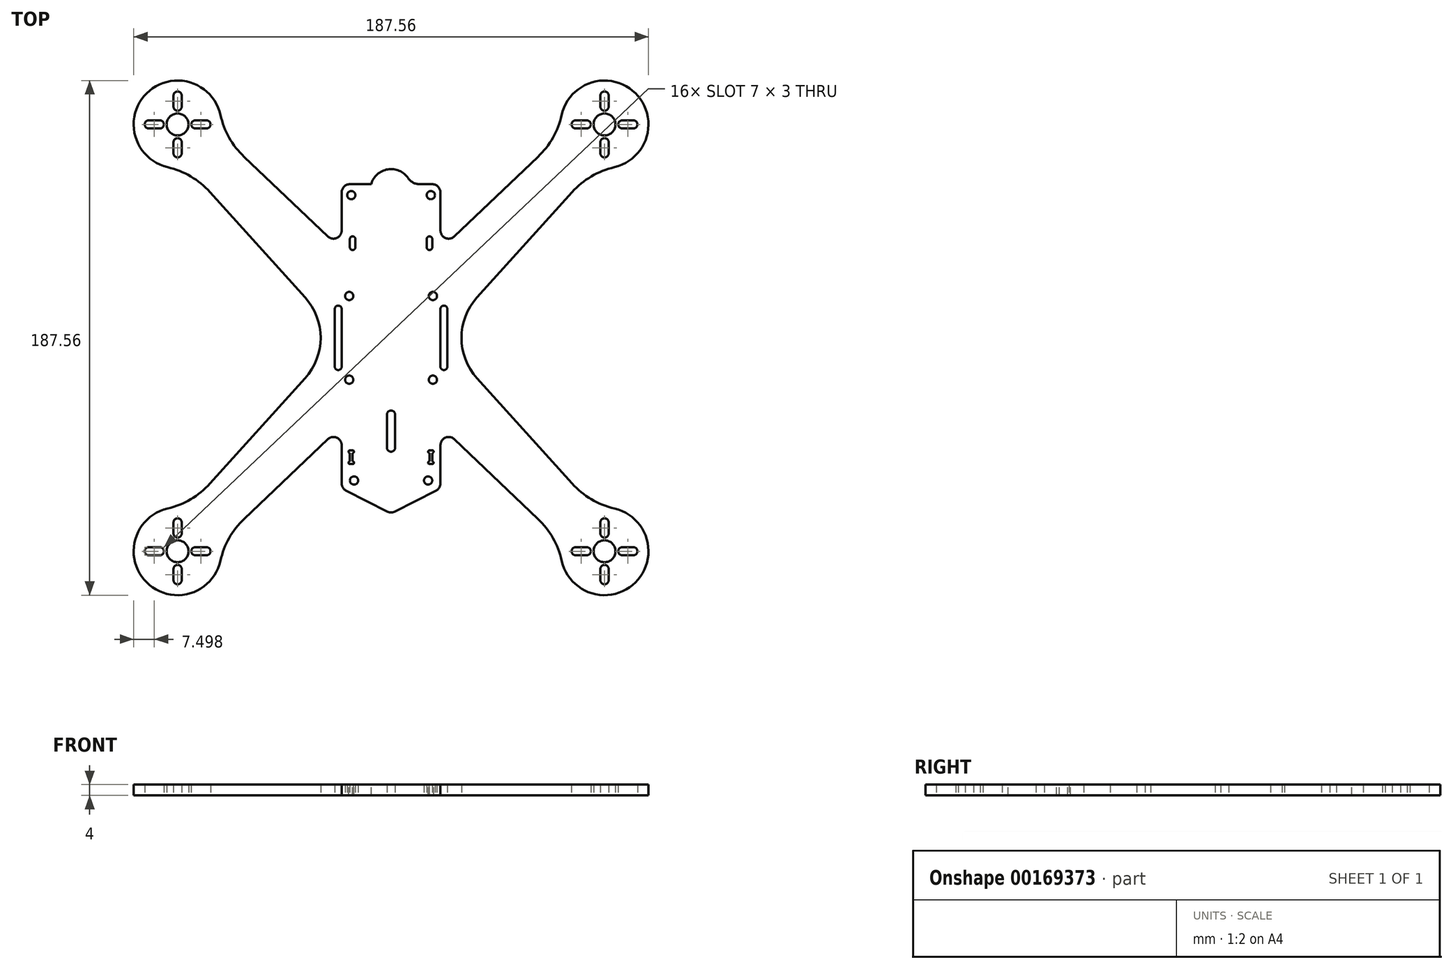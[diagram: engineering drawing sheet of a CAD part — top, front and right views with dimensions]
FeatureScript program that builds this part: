
annotation { "Feature Type Name" : "Feature", "Feature Type Description" : "" }
export const myFeature = defineFeature(function(context is Context, id is Id, definition is map)
    precondition{}
    {
        {
            var Q0;
            Q0=qCreatedBy(makeId("Top.planeOp"),FACE);
            var sketch = newSketch(context, id + "F0", { "sketchPlane" : qUnion([Q0])});
            skLineSegment(sketch, "E0.bottom", {"start": v(-15, 56) * mm, "end": v(15, 56) * mm});
            skLineSegment(sketch, "E0.left", {"start": v(-18, 53) * mm, "end": v(-18, 39.14) * mm});
            skLineSegment(sketch, "E0.right", {"start": v(18, 53) * mm, "end": v(18, 39.14) * mm});
            skCircle(sketch, "E1", {"center": v(0, 0) * mm, "radius": 110 * mm, "construction": true});
            skLineSegment(sketch, "E2", {"start": v(0, 0) * mm, "end": v(-77.78, 77.78) * mm, "construction": true});
            skLineSegment(sketch, "E3", {"start": v(0, 0) * mm, "end": v(-77.78, -77.78) * mm, "construction": true});
            skLineSegment(sketch, "E4", {"start": v(0, 0) * mm, "end": v(77.78, 77.78) * mm, "construction": true});
            skLineSegment(sketch, "E5", {"start": v(0, 0) * mm, "end": v(77.78, -77.78) * mm, "construction": true});
            skCircle(sketch, "E6", {"center": v(-77.78, 77.78) * mm, "radius": 63.5 * mm, "construction": true});
            skCircle(sketch, "E7", {"center": v(-77.78, -77.78) * mm, "radius": 63.5 * mm, "construction": true});
            skCircle(sketch, "E8", {"center": v(77.78, -77.78) * mm, "radius": 63.5 * mm, "construction": true});
            skCircle(sketch, "E9", {"center": v(77.78, 77.78) * mm, "radius": 63.5 * mm, "construction": true});
            skLineSegment(sketch, "E10.trimOffspring", {"start": v(-18, -39.14) * mm, "end": v(-18, -53) * mm});
            skLineSegment(sketch, "E11.trimOffspring", {"start": v(18, -39.14) * mm, "end": v(18, -53) * mm});
            skCircle(sketch, "E12", {"center": v(-15.25, 15.25) * mm, "radius": 1.5 * mm});
            skCircle(sketch, "E13.0.1.0", {"center": v(-15.25, -15.25) * mm, "radius": 1.5 * mm});
            skCircle(sketch, "E13.1.0.0", {"center": v(15.25, 15.25) * mm, "radius": 1.5 * mm});
            skCircle(sketch, "E13.1.1.0", {"center": v(15.25, -15.25) * mm, "radius": 1.5 * mm});
            skLineSegment(sketch, "E13.direction1", {"start": v(-15.25, 15.25) * mm, "end": v(15.25, 15.25) * mm, "construction": true});
            skLineSegment(sketch, "E13.direction2", {"start": v(-15.25, 15.25) * mm, "end": v(-15.25, -15.25) * mm, "construction": true});
            skPoint(sketch, "E14.visualSharp", {"position": v(-18, -32.14) * mm});
            skPoint(sketch, "E15.visualSharp", {"position": v(18, -32.14) * mm});
            skPoint(sketch, "E16.visualSharp", {"position": v(18, 32.14) * mm});
            skPoint(sketch, "E17.visualSharp", {"position": v(-18, 32.14) * mm});
            skCircle(sketch, "E18", {"center": v(-13.5, -52) * mm, "radius": 1.5 * mm});
            skCircle(sketch, "E19", {"center": v(-14.5, 52) * mm, "radius": 1.5 * mm});
            skCircle(sketch, "E20.1.0.0", {"center": v(14.5, 52) * mm, "radius": 1.5 * mm});
            skLineSegment(sketch, "E21", {"start": v(-14.5, 52) * mm, "end": v(14.5, 52) * mm, "construction": true});
            skCircle(sketch, "E22.1.0.0", {"center": v(13.5, -52) * mm, "radius": 1.5 * mm});
            skLineSegment(sketch, "E22.direction1", {"start": v(-13.5, -52) * mm, "end": v(13.5, -52) * mm, "construction": true});
            skPoint(sketch, "E23.visualSharp", {"position": v(-18, 56) * mm});
            skArc(sketch, "E23.filletArc", {"start": v(-15, 56) * mm, "mid": v(-17.12, 55.12) * mm, "end": v(-18, 53) * mm});
            skPoint(sketch, "E24.visualSharp", {"position": v(18, 56) * mm});
            skArc(sketch, "E24.filletArc", {"start": v(18, 53) * mm, "mid": v(17.12, 55.12) * mm, "end": v(15, 56) * mm});
            skArc(sketch, "E25", {"start": v(-81.43, -62.2) * mm, "mid": v(-89.03, -89.16) * mm, "end": v(-62.16, -81.24) * mm});
            skArc(sketch, "E26", {"start": v(62.16, -81.24) * mm, "mid": v(89.03, -89.16) * mm, "end": v(81.43, -62.2) * mm});
            skArc(sketch, "E27", {"start": v(81.43, 62.2) * mm, "mid": v(89.03, 89.16) * mm, "end": v(62.16, 81.24) * mm});
            skArc(sketch, "E28", {"start": v(-62.16, 81.24) * mm, "mid": v(-89.03, 89.16) * mm, "end": v(-81.43, 62.2) * mm});
            skLineSegment(sketch, "E29", {"start": v(-31.33, 14.75) * mm, "end": v(-66, 53.1) * mm});
            skLineSegment(sketch, "E30", {"start": v(-23.07, 36.97) * mm, "end": v(-53.55, 65.99) * mm});
            skPoint(sketch, "E31.visualSharp", {"position": v(-62.19, 74.2) * mm});
            skArc(sketch, "E31.filletArc", {"start": v(-62.16, 81.24) * mm, "mid": v(-59, 72.97) * mm, "end": v(-53.55, 65.99) * mm});
            skPoint(sketch, "E32.visualSharp", {"position": v(-74.2, 62.19) * mm});
            skArc(sketch, "E32.filletArc", {"start": v(-66, 53.1) * mm, "mid": v(-73.02, 58.83) * mm, "end": v(-81.43, 62.2) * mm});
            skLineSegment(sketch, "E33", {"start": v(23.07, 36.97) * mm, "end": v(53.55, 65.99) * mm});
            skLineSegment(sketch, "E34", {"start": v(31.33, 14.75) * mm, "end": v(66, 53.1) * mm});
            skPoint(sketch, "E35.visualSharp", {"position": v(62.19, 74.2) * mm});
            skArc(sketch, "E35.filletArc", {"start": v(53.55, 65.99) * mm, "mid": v(59, 72.97) * mm, "end": v(62.16, 81.24) * mm});
            skPoint(sketch, "E36.visualSharp", {"position": v(74.2, 62.19) * mm});
            skArc(sketch, "E36.filletArc", {"start": v(81.43, 62.2) * mm, "mid": v(73.02, 58.83) * mm, "end": v(66, 53.1) * mm});
            skLineSegment(sketch, "E37", {"start": v(-31.33, -14.75) * mm, "end": v(-66, -53.1) * mm});
            skLineSegment(sketch, "E38", {"start": v(-53.55, -65.99) * mm, "end": v(-23.07, -36.97) * mm});
            skLineSegment(sketch, "E39", {"start": v(23.07, -36.97) * mm, "end": v(53.55, -65.99) * mm});
            skLineSegment(sketch, "E40", {"start": v(66, -53.1) * mm, "end": v(31.33, -14.75) * mm});
            skPoint(sketch, "E41.visualSharp", {"position": v(-74.2, -62.19) * mm});
            skArc(sketch, "E41.filletArc", {"start": v(-81.43, -62.2) * mm, "mid": v(-73.02, -58.83) * mm, "end": v(-66, -53.1) * mm});
            skPoint(sketch, "E42.visualSharp", {"position": v(-62.19, -74.2) * mm});
            skArc(sketch, "E42.filletArc", {"start": v(-53.55, -65.99) * mm, "mid": v(-59, -72.97) * mm, "end": v(-62.16, -81.24) * mm});
            skPoint(sketch, "E43.visualSharp", {"position": v(62.19, -74.2) * mm});
            skArc(sketch, "E43.filletArc", {"start": v(62.16, -81.24) * mm, "mid": v(59, -72.97) * mm, "end": v(53.55, -65.99) * mm});
            skPoint(sketch, "E44.visualSharp", {"position": v(74.2, -62.19) * mm});
            skArc(sketch, "E44.filletArc", {"start": v(66, -53.1) * mm, "mid": v(73.02, -58.83) * mm, "end": v(81.43, -62.2) * mm});
            skCircle(sketch, "E45", {"center": v(-77.78, 77.78) * mm, "radius": 4 * mm});
            skCircle(sketch, "E46", {"center": v(77.78, 77.78) * mm, "radius": 4 * mm});
            skCircle(sketch, "E47", {"center": v(77.78, -77.78) * mm, "radius": 4 * mm});
            skCircle(sketch, "E48", {"center": v(-77.78, -77.78) * mm, "radius": 4 * mm});
            skArc(sketch, "E49", {"start": v(1.5, -28) * mm, "mid": v(0, -26.5) * mm, "end": v(-1.5, -28) * mm});
            skArc(sketch, "E50", {"start": v(-1.5, -40) * mm, "mid": v(0, -41.5) * mm, "end": v(1.5, -40) * mm});
            skLineSegment(sketch, "E51", {"start": v(-1.5, -28) * mm, "end": v(-1.5, -40) * mm});
            skLineSegment(sketch, "E52", {"start": v(1.5, -28) * mm, "end": v(1.5, -40) * mm});
            skArc(sketch, "E53.filletArc", {"start": v(-18, -39.14) * mm, "mid": v(-19.82, -36.38) * mm, "end": v(-23.07, -36.97) * mm});
            skArc(sketch, "E54.filletArc", {"start": v(23.07, -36.97) * mm, "mid": v(19.82, -36.38) * mm, "end": v(18, -39.14) * mm});
            skArc(sketch, "E55.filletArc", {"start": v(-23.07, 36.97) * mm, "mid": v(-19.82, 36.38) * mm, "end": v(-18, 39.14) * mm});
            skArc(sketch, "E56.filletArc", {"start": v(18, 39.14) * mm, "mid": v(19.82, 36.38) * mm, "end": v(23.07, 36.97) * mm});
            skArc(sketch, "E57", {"start": v(-13, 36) * mm, "mid": v(-14, 37) * mm, "end": v(-15, 36) * mm});
            skArc(sketch, "E58", {"start": v(-15, 33) * mm, "mid": v(-14, 32) * mm, "end": v(-13, 33) * mm});
            skLineSegment(sketch, "E59", {"start": v(-14, 36) * mm, "end": v(-14, 33) * mm, "construction": true});
            skLineSegment(sketch, "E60", {"start": v(-15, 36) * mm, "end": v(-15, 33) * mm});
            skLineSegment(sketch, "E61", {"start": v(-13, 36) * mm, "end": v(-13, 33) * mm});
            skLineSegment(sketch, "E62.MirrorCS", {"start": v(14, 36) * mm, "end": v(14, 33) * mm, "construction": true});
            skArc(sketch, "E63.MirrorCS", {"start": v(13, 36) * mm, "mid": v(14, 37) * mm, "end": v(15, 36) * mm});
            skArc(sketch, "E64.MirrorCS", {"start": v(15, 33) * mm, "mid": v(14, 32) * mm, "end": v(13, 33) * mm});
            skLineSegment(sketch, "E65.MirrorCS", {"start": v(13, 36) * mm, "end": v(13, 33) * mm});
            skLineSegment(sketch, "E66.MirrorCS", {"start": v(15, 36) * mm, "end": v(15, 33) * mm});
            skPoint(sketch, "E67.visualSharp", {"position": v(-18, 0) * mm});
            skArc(sketch, "E67.filletArc", {"start": v(-31.33, -14.75) * mm, "mid": v(-25.65, 0) * mm, "end": v(-31.33, 14.75) * mm});
            skPoint(sketch, "E68.visualSharp", {"position": v(18, 0) * mm});
            skArc(sketch, "E68.filletArc", {"start": v(31.33, 14.75) * mm, "mid": v(25.65, 0) * mm, "end": v(31.33, -14.75) * mm});
            skLineSegment(sketch, "E69.left", {"start": v(-20.5, 10.5) * mm, "end": v(-20.5, -10.5) * mm});
            skLineSegment(sketch, "E69.right", {"start": v(-18, 10.5) * mm, "end": v(-18, -10.5) * mm});
            skArc(sketch, "E70", {"start": v(-18, 10.5) * mm, "mid": v(-19.25, 11.75) * mm, "end": v(-20.5, 10.5) * mm});
            skArc(sketch, "E71", {"start": v(-20.5, -10.5) * mm, "mid": v(-19.25, -11.75) * mm, "end": v(-18, -10.5) * mm});
            skArc(sketch, "E72.MirrorCS", {"start": v(20.5, -10.5) * mm, "mid": v(19.25, -11.75) * mm, "end": v(18, -10.5) * mm});
            skLineSegment(sketch, "E73.MirrorCS", {"start": v(20.5, 10.5) * mm, "end": v(20.5, -10.5) * mm});
            skArc(sketch, "E74.MirrorCS", {"start": v(18, 10.5) * mm, "mid": v(19.25, 11.75) * mm, "end": v(20.5, 10.5) * mm});
            skLineSegment(sketch, "E75.MirrorCS", {"start": v(18, 10.5) * mm, "end": v(18, -10.5) * mm});
            skLineSegment(sketch, "E76", {"start": v(-15, -56) * mm, "end": v(15, -56) * mm});
            skPoint(sketch, "E77.visualSharp", {"position": v(-18, -56) * mm});
            skArc(sketch, "E77.filletArc", {"start": v(-18, -53) * mm, "mid": v(-17.12, -55.12) * mm, "end": v(-15, -56) * mm});
            skPoint(sketch, "E78.visualSharp", {"position": v(18, -56) * mm});
            skArc(sketch, "E78.filletArc", {"start": v(15, -56) * mm, "mid": v(17.12, -55.12) * mm, "end": v(18, -53) * mm});
            skLineSegment(sketch, "E79", {"start": v(-77.78, 77.78) * mm, "end": v(-89.03, 89.16) * mm, "construction": true});
            skLineSegment(sketch, "E80", {"start": v(-77.78, 77.78) * mm, "end": v(-89.1, 66.47) * mm, "construction": true});
            skLineSegment(sketch, "E81", {"start": v(-77.78, 77.78) * mm, "end": v(-66.47, 89.1) * mm, "construction": true});
            skArc(sketch, "E82", {"start": v(-79.28, 84.28) * mm, "mid": v(-77.78, 82.78) * mm, "end": v(-76.28, 84.28) * mm});
            skArc(sketch, "E83", {"start": v(-76.28, 88.28) * mm, "mid": v(-77.78, 89.78) * mm, "end": v(-79.28, 88.28) * mm});
            skLineSegment(sketch, "E84", {"start": v(-79.28, 88.28) * mm, "end": v(-79.28, 84.28) * mm});
            skLineSegment(sketch, "E85", {"start": v(-76.28, 88.28) * mm, "end": v(-76.28, 84.28) * mm});
            skLineSegment(sketch, "E86", {"start": v(-77.78, 77.78) * mm, "end": v(-77.78, 93.78) * mm, "construction": true});
            skArc(sketch, "E87.1.0", {"start": v(-88.28, 79.28) * mm, "mid": v(-89.78, 77.78) * mm, "end": v(-88.28, 76.28) * mm});
            skArc(sketch, "E87.1.1", {"start": v(-84.28, 76.28) * mm, "mid": v(-82.78, 77.78) * mm, "end": v(-84.28, 79.28) * mm});
            skLineSegment(sketch, "E87.1.2", {"start": v(-88.28, 79.28) * mm, "end": v(-84.28, 79.28) * mm});
            skLineSegment(sketch, "E87.1.3", {"start": v(-88.28, 76.28) * mm, "end": v(-84.28, 76.28) * mm});
            skArc(sketch, "E87.2.0", {"start": v(-79.28, 67.28) * mm, "mid": v(-77.78, 65.78) * mm, "end": v(-76.28, 67.28) * mm});
            skArc(sketch, "E87.2.1", {"start": v(-76.28, 71.28) * mm, "mid": v(-77.78, 72.78) * mm, "end": v(-79.28, 71.28) * mm});
            skLineSegment(sketch, "E87.2.2", {"start": v(-79.28, 67.28) * mm, "end": v(-79.28, 71.28) * mm});
            skLineSegment(sketch, "E87.2.3", {"start": v(-76.28, 67.28) * mm, "end": v(-76.28, 71.28) * mm});
            skArc(sketch, "E87.3.0", {"start": v(-67.28, 76.28) * mm, "mid": v(-65.78, 77.78) * mm, "end": v(-67.28, 79.28) * mm});
            skArc(sketch, "E87.3.1", {"start": v(-71.28, 79.28) * mm, "mid": v(-72.78, 77.78) * mm, "end": v(-71.28, 76.28) * mm});
            skLineSegment(sketch, "E87.3.2", {"start": v(-67.28, 76.28) * mm, "end": v(-71.28, 76.28) * mm});
            skLineSegment(sketch, "E87.3.3", {"start": v(-67.28, 79.28) * mm, "end": v(-71.28, 79.28) * mm});
            skLineSegment(sketch, "E88.1.0", {"start": v(-88.28, -79.28) * mm, "end": v(-84.28, -79.28) * mm});
            skArc(sketch, "E88.1.1", {"start": v(-88.28, -76.28) * mm, "mid": v(-89.78, -77.78) * mm, "end": v(-88.28, -79.28) * mm});
            skLineSegment(sketch, "E88.1.2", {"start": v(-88.28, -76.28) * mm, "end": v(-84.28, -76.28) * mm});
            skArc(sketch, "E88.1.3", {"start": v(-84.28, -79.28) * mm, "mid": v(-82.78, -77.78) * mm, "end": v(-84.28, -76.28) * mm});
            skArc(sketch, "E88.1.4", {"start": v(-76.28, -67.28) * mm, "mid": v(-77.78, -65.78) * mm, "end": v(-79.28, -67.28) * mm});
            skLineSegment(sketch, "E88.1.5", {"start": v(-79.28, -67.28) * mm, "end": v(-79.28, -71.28) * mm});
            skLineSegment(sketch, "E88.1.6", {"start": v(-76.28, -67.28) * mm, "end": v(-76.28, -71.28) * mm});
            skArc(sketch, "E88.1.7", {"start": v(-79.28, -71.28) * mm, "mid": v(-77.78, -72.78) * mm, "end": v(-76.28, -71.28) * mm});
            skLineSegment(sketch, "E88.1.8", {"start": v(-67.28, -79.28) * mm, "end": v(-71.28, -79.28) * mm});
            skArc(sketch, "E88.1.9", {"start": v(-71.28, -76.28) * mm, "mid": v(-72.78, -77.78) * mm, "end": v(-71.28, -79.28) * mm});
            skLineSegment(sketch, "E88.1.10", {"start": v(-67.28, -76.28) * mm, "end": v(-71.28, -76.28) * mm});
            skArc(sketch, "E88.1.11", {"start": v(-67.28, -79.28) * mm, "mid": v(-65.78, -77.78) * mm, "end": v(-67.28, -76.28) * mm});
            skArc(sketch, "E88.1.12", {"start": v(-76.28, -84.28) * mm, "mid": v(-77.78, -82.78) * mm, "end": v(-79.28, -84.28) * mm});
            skLineSegment(sketch, "E88.1.13", {"start": v(-76.28, -88.28) * mm, "end": v(-76.28, -84.28) * mm});
            skLineSegment(sketch, "E88.1.14", {"start": v(-79.28, -88.28) * mm, "end": v(-79.28, -84.28) * mm});
            skArc(sketch, "E88.1.15", {"start": v(-79.28, -88.28) * mm, "mid": v(-77.78, -89.78) * mm, "end": v(-76.28, -88.28) * mm});
            skLineSegment(sketch, "E88.2.0", {"start": v(79.28, -88.28) * mm, "end": v(79.28, -84.28) * mm});
            skArc(sketch, "E88.2.1", {"start": v(76.28, -88.28) * mm, "mid": v(77.78, -89.78) * mm, "end": v(79.28, -88.28) * mm});
            skLineSegment(sketch, "E88.2.2", {"start": v(76.28, -88.28) * mm, "end": v(76.28, -84.28) * mm});
            skArc(sketch, "E88.2.3", {"start": v(79.28, -84.28) * mm, "mid": v(77.78, -82.78) * mm, "end": v(76.28, -84.28) * mm});
            skArc(sketch, "E88.2.4", {"start": v(67.28, -76.28) * mm, "mid": v(65.78, -77.78) * mm, "end": v(67.28, -79.28) * mm});
            skLineSegment(sketch, "E88.2.5", {"start": v(67.28, -79.28) * mm, "end": v(71.28, -79.28) * mm});
            skLineSegment(sketch, "E88.2.6", {"start": v(67.28, -76.28) * mm, "end": v(71.28, -76.28) * mm});
            skArc(sketch, "E88.2.7", {"start": v(71.28, -79.28) * mm, "mid": v(72.78, -77.78) * mm, "end": v(71.28, -76.28) * mm});
            skLineSegment(sketch, "E88.2.8", {"start": v(79.28, -67.28) * mm, "end": v(79.28, -71.28) * mm});
            skArc(sketch, "E88.2.9", {"start": v(76.28, -71.28) * mm, "mid": v(77.78, -72.78) * mm, "end": v(79.28, -71.28) * mm});
            skLineSegment(sketch, "E88.2.10", {"start": v(76.28, -67.28) * mm, "end": v(76.28, -71.28) * mm});
            skArc(sketch, "E88.2.11", {"start": v(79.28, -67.28) * mm, "mid": v(77.78, -65.78) * mm, "end": v(76.28, -67.28) * mm});
            skArc(sketch, "E88.2.12", {"start": v(84.28, -76.28) * mm, "mid": v(82.78, -77.78) * mm, "end": v(84.28, -79.28) * mm});
            skLineSegment(sketch, "E88.2.13", {"start": v(88.28, -76.28) * mm, "end": v(84.28, -76.28) * mm});
            skLineSegment(sketch, "E88.2.14", {"start": v(88.28, -79.28) * mm, "end": v(84.28, -79.28) * mm});
            skArc(sketch, "E88.2.15", {"start": v(88.28, -79.28) * mm, "mid": v(89.78, -77.78) * mm, "end": v(88.28, -76.28) * mm});
            skLineSegment(sketch, "E88.3.0", {"start": v(88.28, 79.28) * mm, "end": v(84.28, 79.28) * mm});
            skArc(sketch, "E88.3.1", {"start": v(88.28, 76.28) * mm, "mid": v(89.78, 77.78) * mm, "end": v(88.28, 79.28) * mm});
            skLineSegment(sketch, "E88.3.2", {"start": v(88.28, 76.28) * mm, "end": v(84.28, 76.28) * mm});
            skArc(sketch, "E88.3.3", {"start": v(84.28, 79.28) * mm, "mid": v(82.78, 77.78) * mm, "end": v(84.28, 76.28) * mm});
            skArc(sketch, "E88.3.4", {"start": v(76.28, 67.28) * mm, "mid": v(77.78, 65.78) * mm, "end": v(79.28, 67.28) * mm});
            skLineSegment(sketch, "E88.3.5", {"start": v(79.28, 67.28) * mm, "end": v(79.28, 71.28) * mm});
            skLineSegment(sketch, "E88.3.6", {"start": v(76.28, 67.28) * mm, "end": v(76.28, 71.28) * mm});
            skArc(sketch, "E88.3.7", {"start": v(79.28, 71.28) * mm, "mid": v(77.78, 72.78) * mm, "end": v(76.28, 71.28) * mm});
            skLineSegment(sketch, "E88.3.8", {"start": v(67.28, 79.28) * mm, "end": v(71.28, 79.28) * mm});
            skArc(sketch, "E88.3.9", {"start": v(71.28, 76.28) * mm, "mid": v(72.78, 77.78) * mm, "end": v(71.28, 79.28) * mm});
            skLineSegment(sketch, "E88.3.10", {"start": v(67.28, 76.28) * mm, "end": v(71.28, 76.28) * mm});
            skArc(sketch, "E88.3.11", {"start": v(67.28, 79.28) * mm, "mid": v(65.78, 77.78) * mm, "end": v(67.28, 76.28) * mm});
            skArc(sketch, "E88.3.12", {"start": v(76.28, 84.28) * mm, "mid": v(77.78, 82.78) * mm, "end": v(79.28, 84.28) * mm});
            skLineSegment(sketch, "E88.3.13", {"start": v(76.28, 88.28) * mm, "end": v(76.28, 84.28) * mm});
            skLineSegment(sketch, "E88.3.14", {"start": v(79.28, 88.28) * mm, "end": v(79.28, 84.28) * mm});
            skArc(sketch, "E88.3.15", {"start": v(79.28, 88.28) * mm, "mid": v(77.78, 89.78) * mm, "end": v(76.28, 88.28) * mm});
            skLineSegment(sketch, "E89", {"start": v(-93.78, -77.78) * mm, "end": v(-61.17, -77.78) * mm, "construction": true});
            skLineSegment(sketch, "E90", {"start": v(-77.78, -93.78) * mm, "end": v(-77.78, -61.1) * mm, "construction": true});
            skPoint(sketch, "E90.endSnap0", {"position": v(-77.78, -65.78) * mm});
            skSolve(sketch);
        }
        {
            var Q0;
            Q0=qSketchRegion(id+"F0",true);
            extrude(context, id + "F1", {"entities" : qUnion([Q0]), "depth" : 4 * mm});
        }
        {
            var Q0;
            Q0=makeQuery(id+"F1.opExtrude","CAP_FACE",FACE,{"disambiguationData":[OSD([sQuery(id+"F0.wireOp",EDGE,"E0.bottom"),sQuery(id+"F0.wireOp",EDGE,"E0.left"),sQuery(id+"F0.wireOp",EDGE,"E0.right"),sQuery(id+"F0.wireOp",EDGE,"E10.trimOffspring"),sQuery(id+"F0.wireOp",EDGE,"E11.trimOffspring"),sQuery(id+"F0.wireOp",EDGE,"E12"),sQuery(id+"F0.wireOp",EDGE,"E13.0.1.0"),sQuery(id+"F0.wireOp",EDGE,"E13.1.0.0"),sQuery(id+"F0.wireOp",EDGE,"E13.1.1.0"),sQuery(id+"F0.wireOp",EDGE,"E18"),sQuery(id+"F0.wireOp",EDGE,"E19"),sQuery(id+"F0.wireOp",EDGE,"E20.1.0.0"),sQuery(id+"F0.wireOp",EDGE,"E22.1.0.0"),sQuery(id+"F0.wireOp",EDGE,"E23.filletArc"),sQuery(id+"F0.wireOp",EDGE,"E24.filletArc"),sQuery(id+"F0.wireOp",EDGE,"E25"),sQuery(id+"F0.wireOp",EDGE,"E26"),sQuery(id+"F0.wireOp",EDGE,"E27"),sQuery(id+"F0.wireOp",EDGE,"E28"),sQuery(id+"F0.wireOp",EDGE,"E29"),sQuery(id+"F0.wireOp",EDGE,"E30"),sQuery(id+"F0.wireOp",EDGE,"E31.filletArc"),sQuery(id+"F0.wireOp",EDGE,"E32.filletArc"),sQuery(id+"F0.wireOp",EDGE,"E33"),sQuery(id+"F0.wireOp",EDGE,"E34"),sQuery(id+"F0.wireOp",EDGE,"E35.filletArc"),sQuery(id+"F0.wireOp",EDGE,"E36.filletArc"),sQuery(id+"F0.wireOp",EDGE,"E37"),sQuery(id+"F0.wireOp",EDGE,"E38"),sQuery(id+"F0.wireOp",EDGE,"E39"),sQuery(id+"F0.wireOp",EDGE,"E40"),sQuery(id+"F0.wireOp",EDGE,"E41.filletArc"),sQuery(id+"F0.wireOp",EDGE,"E42.filletArc"),sQuery(id+"F0.wireOp",EDGE,"E43.filletArc"),sQuery(id+"F0.wireOp",EDGE,"E44.filletArc"),sQuery(id+"F0.wireOp",EDGE,"E45"),sQuery(id+"F0.wireOp",EDGE,"E46"),sQuery(id+"F0.wireOp",EDGE,"E47"),sQuery(id+"F0.wireOp",EDGE,"E48"),sQuery(id+"F0.wireOp",EDGE,"E49"),sQuery(id+"F0.wireOp",EDGE,"E50"),sQuery(id+"F0.wireOp",EDGE,"E51"),sQuery(id+"F0.wireOp",EDGE,"E52"),sQuery(id+"F0.wireOp",EDGE,"E53.filletArc"),sQuery(id+"F0.wireOp",EDGE,"E54.filletArc"),sQuery(id+"F0.wireOp",EDGE,"E55.filletArc"),sQuery(id+"F0.wireOp",EDGE,"E56.filletArc"),sQuery(id+"F0.wireOp",EDGE,"E57"),sQuery(id+"F0.wireOp",EDGE,"E58"),sQuery(id+"F0.wireOp",EDGE,"E60"),sQuery(id+"F0.wireOp",EDGE,"E61"),sQuery(id+"F0.wireOp",EDGE,"E63.MirrorCS"),sQuery(id+"F0.wireOp",EDGE,"E64.MirrorCS"),sQuery(id+"F0.wireOp",EDGE,"E65.MirrorCS"),sQuery(id+"F0.wireOp",EDGE,"E66.MirrorCS"),sQuery(id+"F0.wireOp",EDGE,"E67.filletArc"),sQuery(id+"F0.wireOp",EDGE,"E68.filletArc"),sQuery(id+"F0.wireOp",EDGE,"E69.left"),sQuery(id+"F0.wireOp",EDGE,"E69.right"),sQuery(id+"F0.wireOp",EDGE,"E70"),sQuery(id+"F0.wireOp",EDGE,"E71"),sQuery(id+"F0.wireOp",EDGE,"E72.MirrorCS"),sQuery(id+"F0.wireOp",EDGE,"E73.MirrorCS"),sQuery(id+"F0.wireOp",EDGE,"E74.MirrorCS"),sQuery(id+"F0.wireOp",EDGE,"E75.MirrorCS"),sQuery(id+"F0.wireOp",EDGE,"E76"),sQuery(id+"F0.wireOp",EDGE,"E77.filletArc"),sQuery(id+"F0.wireOp",EDGE,"E78.filletArc"),sQuery(id+"F0.wireOp",EDGE,"E82"),sQuery(id+"F0.wireOp",EDGE,"E83"),sQuery(id+"F0.wireOp",EDGE,"E84"),sQuery(id+"F0.wireOp",EDGE,"E85"),sQuery(id+"F0.wireOp",EDGE,"E87.1.0"),sQuery(id+"F0.wireOp",EDGE,"E87.1.1"),sQuery(id+"F0.wireOp",EDGE,"E87.1.2"),sQuery(id+"F0.wireOp",EDGE,"E87.1.3"),sQuery(id+"F0.wireOp",EDGE,"E87.2.0"),sQuery(id+"F0.wireOp",EDGE,"E87.2.1"),sQuery(id+"F0.wireOp",EDGE,"E87.2.2"),sQuery(id+"F0.wireOp",EDGE,"E87.2.3"),sQuery(id+"F0.wireOp",EDGE,"E87.3.0"),sQuery(id+"F0.wireOp",EDGE,"E87.3.1"),sQuery(id+"F0.wireOp",EDGE,"E87.3.2"),sQuery(id+"F0.wireOp",EDGE,"E87.3.3"),sQuery(id+"F0.wireOp",EDGE,"E88.1.0"),sQuery(id+"F0.wireOp",EDGE,"E88.1.1"),sQuery(id+"F0.wireOp",EDGE,"E88.1.2"),sQuery(id+"F0.wireOp",EDGE,"E88.1.3"),sQuery(id+"F0.wireOp",EDGE,"E88.1.4"),sQuery(id+"F0.wireOp",EDGE,"E88.1.5"),sQuery(id+"F0.wireOp",EDGE,"E88.1.6"),sQuery(id+"F0.wireOp",EDGE,"E88.1.7"),sQuery(id+"F0.wireOp",EDGE,"E88.1.8"),sQuery(id+"F0.wireOp",EDGE,"E88.1.9"),sQuery(id+"F0.wireOp",EDGE,"E88.1.10"),sQuery(id+"F0.wireOp",EDGE,"E88.1.11"),sQuery(id+"F0.wireOp",EDGE,"E88.1.12"),sQuery(id+"F0.wireOp",EDGE,"E88.1.13"),sQuery(id+"F0.wireOp",EDGE,"E88.1.14"),sQuery(id+"F0.wireOp",EDGE,"E88.1.15"),sQuery(id+"F0.wireOp",EDGE,"E88.2.0"),sQuery(id+"F0.wireOp",EDGE,"E88.2.1"),sQuery(id+"F0.wireOp",EDGE,"E88.2.2"),sQuery(id+"F0.wireOp",EDGE,"E88.2.3"),sQuery(id+"F0.wireOp",EDGE,"E88.2.4"),sQuery(id+"F0.wireOp",EDGE,"E88.2.5"),sQuery(id+"F0.wireOp",EDGE,"E88.2.6"),sQuery(id+"F0.wireOp",EDGE,"E88.2.7"),sQuery(id+"F0.wireOp",EDGE,"E88.2.8"),sQuery(id+"F0.wireOp",EDGE,"E88.2.9"),sQuery(id+"F0.wireOp",EDGE,"E88.2.10"),sQuery(id+"F0.wireOp",EDGE,"E88.2.11"),sQuery(id+"F0.wireOp",EDGE,"E88.2.12"),sQuery(id+"F0.wireOp",EDGE,"E88.2.13"),sQuery(id+"F0.wireOp",EDGE,"E88.2.14"),sQuery(id+"F0.wireOp",EDGE,"E88.2.15"),sQuery(id+"F0.wireOp",EDGE,"E88.3.0"),sQuery(id+"F0.wireOp",EDGE,"E88.3.1"),sQuery(id+"F0.wireOp",EDGE,"E88.3.2"),sQuery(id+"F0.wireOp",EDGE,"E88.3.3"),sQuery(id+"F0.wireOp",EDGE,"E88.3.4"),sQuery(id+"F0.wireOp",EDGE,"E88.3.5"),sQuery(id+"F0.wireOp",EDGE,"E88.3.6"),sQuery(id+"F0.wireOp",EDGE,"E88.3.7"),sQuery(id+"F0.wireOp",EDGE,"E88.3.8"),sQuery(id+"F0.wireOp",EDGE,"E88.3.9"),sQuery(id+"F0.wireOp",EDGE,"E88.3.10"),sQuery(id+"F0.wireOp",EDGE,"E88.3.11"),sQuery(id+"F0.wireOp",EDGE,"E88.3.12"),sQuery(id+"F0.wireOp",EDGE,"E88.3.13"),sQuery(id+"F0.wireOp",EDGE,"E88.3.14"),sQuery(id+"F0.wireOp",EDGE,"E88.3.15")])],"isStart":false});
            var sketch = newSketch(context, id + "F2", { "sketchPlane" : qUnion([Q0])});
            skLineSegment(sketch, "E91.bottom", {"start": v(-15, -41) * mm, "end": v(-14, -41) * mm});
            skLineSegment(sketch, "E91.top", {"start": v(-15, -46) * mm, "end": v(-14, -46) * mm});
            skLineSegment(sketch, "E91.right", {"start": v(-14, -42) * mm, "end": v(-14, -45) * mm});
            skArc(sketch, "E92", {"start": v(-14, -46) * mm, "mid": v(-13.5, -45.5) * mm, "end": v(-14, -45) * mm});
            skArc(sketch, "E93", {"start": v(-15, -45) * mm, "mid": v(-15.5, -45.5) * mm, "end": v(-15, -46) * mm});
            skArc(sketch, "E94", {"start": v(-15, -41) * mm, "mid": v(-15.5, -41.5) * mm, "end": v(-15, -42) * mm});
            skArc(sketch, "E95", {"start": v(-14, -42) * mm, "mid": v(-13.5, -41.5) * mm, "end": v(-14, -41) * mm});
            skLineSegment(sketch, "E96.trimOffspring", {"start": v(-15, -42) * mm, "end": v(-15, -45) * mm});
            skArc(sketch, "E97.MirrorCS", {"start": v(15, -45) * mm, "mid": v(15.5, -45.5) * mm, "end": v(15, -46) * mm});
            skLineSegment(sketch, "E98.MirrorCS", {"start": v(15, -46) * mm, "end": v(14, -46) * mm});
            skLineSegment(sketch, "E99.MirrorCS", {"start": v(15, -41) * mm, "end": v(14, -41) * mm});
            skArc(sketch, "E100.MirrorCS", {"start": v(14, -46) * mm, "mid": v(13.5, -45.5) * mm, "end": v(14, -45) * mm});
            skArc(sketch, "E101.MirrorCS", {"start": v(14, -42) * mm, "mid": v(13.5, -41.5) * mm, "end": v(14, -41) * mm});
            skArc(sketch, "E102.MirrorCS", {"start": v(15, -41) * mm, "mid": v(15.5, -41.5) * mm, "end": v(15, -42) * mm});
            skLineSegment(sketch, "E103.MirrorCS", {"start": v(15, -42) * mm, "end": v(15, -45) * mm});
            skLineSegment(sketch, "E104.MirrorCS", {"start": v(14, -42) * mm, "end": v(14, -45) * mm});
            skSolve(sketch);
        }
        {
            var Q0;
            Q0=qSketchRegion(id+"F2",true);
            extrude(context, id + "F3", {"entities" : qUnion([Q0]), "operationType" : NewBodyOperationType.REMOVE, "endBound" : BoundingType.THROUGH_ALL, "oppositeDirection" : true, "depth" : 25 * mm});
        }
        {
            var Q0;
            Q0=makeQuery(id+"F1.opExtrude","CAP_FACE",FACE,{"disambiguationData":[OSD([sQuery(id+"F0.wireOp",EDGE,"E0.bottom"),sQuery(id+"F0.wireOp",EDGE,"E0.left"),sQuery(id+"F0.wireOp",EDGE,"E0.right"),sQuery(id+"F0.wireOp",EDGE,"E10.trimOffspring"),sQuery(id+"F0.wireOp",EDGE,"E11.trimOffspring"),sQuery(id+"F0.wireOp",EDGE,"E12"),sQuery(id+"F0.wireOp",EDGE,"E13.0.1.0"),sQuery(id+"F0.wireOp",EDGE,"E13.1.0.0"),sQuery(id+"F0.wireOp",EDGE,"E13.1.1.0"),sQuery(id+"F0.wireOp",EDGE,"E18"),sQuery(id+"F0.wireOp",EDGE,"E19"),sQuery(id+"F0.wireOp",EDGE,"E20.1.0.0"),sQuery(id+"F0.wireOp",EDGE,"E22.1.0.0"),sQuery(id+"F0.wireOp",EDGE,"E23.filletArc"),sQuery(id+"F0.wireOp",EDGE,"E24.filletArc"),sQuery(id+"F0.wireOp",EDGE,"E25"),sQuery(id+"F0.wireOp",EDGE,"E26"),sQuery(id+"F0.wireOp",EDGE,"E27"),sQuery(id+"F0.wireOp",EDGE,"E28"),sQuery(id+"F0.wireOp",EDGE,"E29"),sQuery(id+"F0.wireOp",EDGE,"E30"),sQuery(id+"F0.wireOp",EDGE,"E31.filletArc"),sQuery(id+"F0.wireOp",EDGE,"E32.filletArc"),sQuery(id+"F0.wireOp",EDGE,"E33"),sQuery(id+"F0.wireOp",EDGE,"E34"),sQuery(id+"F0.wireOp",EDGE,"E35.filletArc"),sQuery(id+"F0.wireOp",EDGE,"E36.filletArc"),sQuery(id+"F0.wireOp",EDGE,"E37"),sQuery(id+"F0.wireOp",EDGE,"E38"),sQuery(id+"F0.wireOp",EDGE,"E39"),sQuery(id+"F0.wireOp",EDGE,"E40"),sQuery(id+"F0.wireOp",EDGE,"E41.filletArc"),sQuery(id+"F0.wireOp",EDGE,"E42.filletArc"),sQuery(id+"F0.wireOp",EDGE,"E43.filletArc"),sQuery(id+"F0.wireOp",EDGE,"E44.filletArc"),sQuery(id+"F0.wireOp",EDGE,"E45"),sQuery(id+"F0.wireOp",EDGE,"E46"),sQuery(id+"F0.wireOp",EDGE,"E47"),sQuery(id+"F0.wireOp",EDGE,"E48"),sQuery(id+"F0.wireOp",EDGE,"E49"),sQuery(id+"F0.wireOp",EDGE,"E50"),sQuery(id+"F0.wireOp",EDGE,"E51"),sQuery(id+"F0.wireOp",EDGE,"E52"),sQuery(id+"F0.wireOp",EDGE,"E53.filletArc"),sQuery(id+"F0.wireOp",EDGE,"E54.filletArc"),sQuery(id+"F0.wireOp",EDGE,"E55.filletArc"),sQuery(id+"F0.wireOp",EDGE,"E56.filletArc"),sQuery(id+"F0.wireOp",EDGE,"E57"),sQuery(id+"F0.wireOp",EDGE,"E58"),sQuery(id+"F0.wireOp",EDGE,"E60"),sQuery(id+"F0.wireOp",EDGE,"E61"),sQuery(id+"F0.wireOp",EDGE,"E63.MirrorCS"),sQuery(id+"F0.wireOp",EDGE,"E64.MirrorCS"),sQuery(id+"F0.wireOp",EDGE,"E65.MirrorCS"),sQuery(id+"F0.wireOp",EDGE,"E66.MirrorCS"),sQuery(id+"F0.wireOp",EDGE,"E67.filletArc"),sQuery(id+"F0.wireOp",EDGE,"E68.filletArc"),sQuery(id+"F0.wireOp",EDGE,"E69.left"),sQuery(id+"F0.wireOp",EDGE,"E69.right"),sQuery(id+"F0.wireOp",EDGE,"E70"),sQuery(id+"F0.wireOp",EDGE,"E71"),sQuery(id+"F0.wireOp",EDGE,"E72.MirrorCS"),sQuery(id+"F0.wireOp",EDGE,"E73.MirrorCS"),sQuery(id+"F0.wireOp",EDGE,"E74.MirrorCS"),sQuery(id+"F0.wireOp",EDGE,"E75.MirrorCS"),sQuery(id+"F0.wireOp",EDGE,"E76"),sQuery(id+"F0.wireOp",EDGE,"E77.filletArc"),sQuery(id+"F0.wireOp",EDGE,"E78.filletArc"),sQuery(id+"F0.wireOp",EDGE,"E82"),sQuery(id+"F0.wireOp",EDGE,"E83"),sQuery(id+"F0.wireOp",EDGE,"E84"),sQuery(id+"F0.wireOp",EDGE,"E85"),sQuery(id+"F0.wireOp",EDGE,"E87.1.0"),sQuery(id+"F0.wireOp",EDGE,"E87.1.1"),sQuery(id+"F0.wireOp",EDGE,"E87.1.2"),sQuery(id+"F0.wireOp",EDGE,"E87.1.3"),sQuery(id+"F0.wireOp",EDGE,"E87.2.0"),sQuery(id+"F0.wireOp",EDGE,"E87.2.1"),sQuery(id+"F0.wireOp",EDGE,"E87.2.2"),sQuery(id+"F0.wireOp",EDGE,"E87.2.3"),sQuery(id+"F0.wireOp",EDGE,"E87.3.0"),sQuery(id+"F0.wireOp",EDGE,"E87.3.1"),sQuery(id+"F0.wireOp",EDGE,"E87.3.2"),sQuery(id+"F0.wireOp",EDGE,"E87.3.3"),sQuery(id+"F0.wireOp",EDGE,"E88.1.0"),sQuery(id+"F0.wireOp",EDGE,"E88.1.1"),sQuery(id+"F0.wireOp",EDGE,"E88.1.2"),sQuery(id+"F0.wireOp",EDGE,"E88.1.3"),sQuery(id+"F0.wireOp",EDGE,"E88.1.4"),sQuery(id+"F0.wireOp",EDGE,"E88.1.5"),sQuery(id+"F0.wireOp",EDGE,"E88.1.6"),sQuery(id+"F0.wireOp",EDGE,"E88.1.7"),sQuery(id+"F0.wireOp",EDGE,"E88.1.8"),sQuery(id+"F0.wireOp",EDGE,"E88.1.9"),sQuery(id+"F0.wireOp",EDGE,"E88.1.10"),sQuery(id+"F0.wireOp",EDGE,"E88.1.11"),sQuery(id+"F0.wireOp",EDGE,"E88.1.12"),sQuery(id+"F0.wireOp",EDGE,"E88.1.13"),sQuery(id+"F0.wireOp",EDGE,"E88.1.14"),sQuery(id+"F0.wireOp",EDGE,"E88.1.15"),sQuery(id+"F0.wireOp",EDGE,"E88.2.0"),sQuery(id+"F0.wireOp",EDGE,"E88.2.1"),sQuery(id+"F0.wireOp",EDGE,"E88.2.2"),sQuery(id+"F0.wireOp",EDGE,"E88.2.3"),sQuery(id+"F0.wireOp",EDGE,"E88.2.4"),sQuery(id+"F0.wireOp",EDGE,"E88.2.5"),sQuery(id+"F0.wireOp",EDGE,"E88.2.6"),sQuery(id+"F0.wireOp",EDGE,"E88.2.7"),sQuery(id+"F0.wireOp",EDGE,"E88.2.8"),sQuery(id+"F0.wireOp",EDGE,"E88.2.9"),sQuery(id+"F0.wireOp",EDGE,"E88.2.10"),sQuery(id+"F0.wireOp",EDGE,"E88.2.11"),sQuery(id+"F0.wireOp",EDGE,"E88.2.12"),sQuery(id+"F0.wireOp",EDGE,"E88.2.13"),sQuery(id+"F0.wireOp",EDGE,"E88.2.14"),sQuery(id+"F0.wireOp",EDGE,"E88.2.15"),sQuery(id+"F0.wireOp",EDGE,"E88.3.0"),sQuery(id+"F0.wireOp",EDGE,"E88.3.1"),sQuery(id+"F0.wireOp",EDGE,"E88.3.2"),sQuery(id+"F0.wireOp",EDGE,"E88.3.3"),sQuery(id+"F0.wireOp",EDGE,"E88.3.4"),sQuery(id+"F0.wireOp",EDGE,"E88.3.5"),sQuery(id+"F0.wireOp",EDGE,"E88.3.6"),sQuery(id+"F0.wireOp",EDGE,"E88.3.7"),sQuery(id+"F0.wireOp",EDGE,"E88.3.8"),sQuery(id+"F0.wireOp",EDGE,"E88.3.9"),sQuery(id+"F0.wireOp",EDGE,"E88.3.10"),sQuery(id+"F0.wireOp",EDGE,"E88.3.11"),sQuery(id+"F0.wireOp",EDGE,"E88.3.12"),sQuery(id+"F0.wireOp",EDGE,"E88.3.13"),sQuery(id+"F0.wireOp",EDGE,"E88.3.14"),sQuery(id+"F0.wireOp",EDGE,"E88.3.15")])],"isStart":false});
            var sketch = newSketch(context, id + "F4", { "sketchPlane" : qUnion([Q0])});
            skLineSegment(sketch, "E105", {"start": v(-16.36, -55.67) * mm, "end": v(-1.36, -63.3) * mm});
            skLineSegment(sketch, "E106", {"start": v(1.36, -63.3) * mm, "end": v(16.36, -55.67) * mm});
            skPoint(sketch, "E107.visualSharp", {"position": v(0, -64) * mm});
            skArc(sketch, "E107.filletArc", {"start": v(-1.36, -63.3) * mm, "mid": v(0, -63.63) * mm, "end": v(1.36, -63.3) * mm});
            skCircle(sketch, "E108", {"center": v(0, 54) * mm, "radius": 7.5 * mm});
            skSolve(sketch);
        }
        {
            var Q0;
            {var subQ2=sQuery(id+"F4.wireOp",EDGE,"E105");Q0=makeQuery(id+"F4.imprint","IMPRINT",FACE,{"disambiguationData":[TD([[makeQuery(id+"F4.imprint","IMPRINT",EDGE,{"derivedFrom":subQ2}),1.0]])]});}
            var Q1;
            {var subQ0=sQuery(id+"F4.wireOp",EDGE,"E108");var subQ1=makeQuery(id+"F1.opExtrude","CAP_EDGE",EDGE,{"disambiguationData":[OSD([sQuery(id+"F0.wireOp",EDGE,"E0.bottom")])],"isStart":false});var subQ2=makeQuery(id+"F4.imprint","INTERSECT",VERTEX,{"disambiguationData":[OD(0.0)],"derivedFrom":[subQ1,subQ0]});Q1=makeQuery(id+"F4.imprint","IMPRINT",FACE,{"disambiguationData":[TD([[makeQuery(id+"F4.imprint","IMPRINT",EDGE,{"disambiguationData":[TD([[subQ2,1.0]])],"derivedFrom":subQ0}),1.0]])]});}
            extrude(context, id + "F5", {"entities" : qUnion([Q0, Q1]), "operationType" : NewBodyOperationType.ADD, "oppositeDirection" : true, "depth" : 4 * mm});
        }
        {
            var Q0;
            {var subQ0=sQuery(id+"F4.wireOp",EDGE,"E108");var subQ1=sQuery(id+"F0.wireOp",EDGE,"E0.bottom");Q0=makeQuery(id+"F5.opExtrude","SWEPT_EDGE",EDGE,{"disambiguationData":[OSD([subQ1,subQ0]),TDD([makeQuery(id+"F4.imprint","INTERSECT",VERTEX,{"disambiguationData":[OD(0.0)],"derivedFrom":[makeQuery(id+"F1.opExtrude","CAP_EDGE",EDGE,{"disambiguationData":[OSD([subQ1])],"isStart":false}),subQ0]})])]});}
            var Q1;
            {var subQ0=sQuery(id+"F4.wireOp",EDGE,"E108");var subQ1=sQuery(id+"F0.wireOp",EDGE,"E0.bottom");Q1=makeQuery(id+"F5.opExtrude","SWEPT_EDGE",EDGE,{"disambiguationData":[OSD([subQ1,subQ0]),TDD([makeQuery(id+"F4.imprint","INTERSECT",VERTEX,{"disambiguationData":[OD(1.0)],"derivedFrom":[makeQuery(id+"F1.opExtrude","CAP_EDGE",EDGE,{"disambiguationData":[OSD([subQ1])],"isStart":false}),subQ0]})])]});}
            fillet(context, id + "F6", {"entities" : qUnion([Q0, Q1]), "radius" : 5 * mm, "tangentPropagation" : true, "allowEdgeOverflow" : false});
        }
    });
